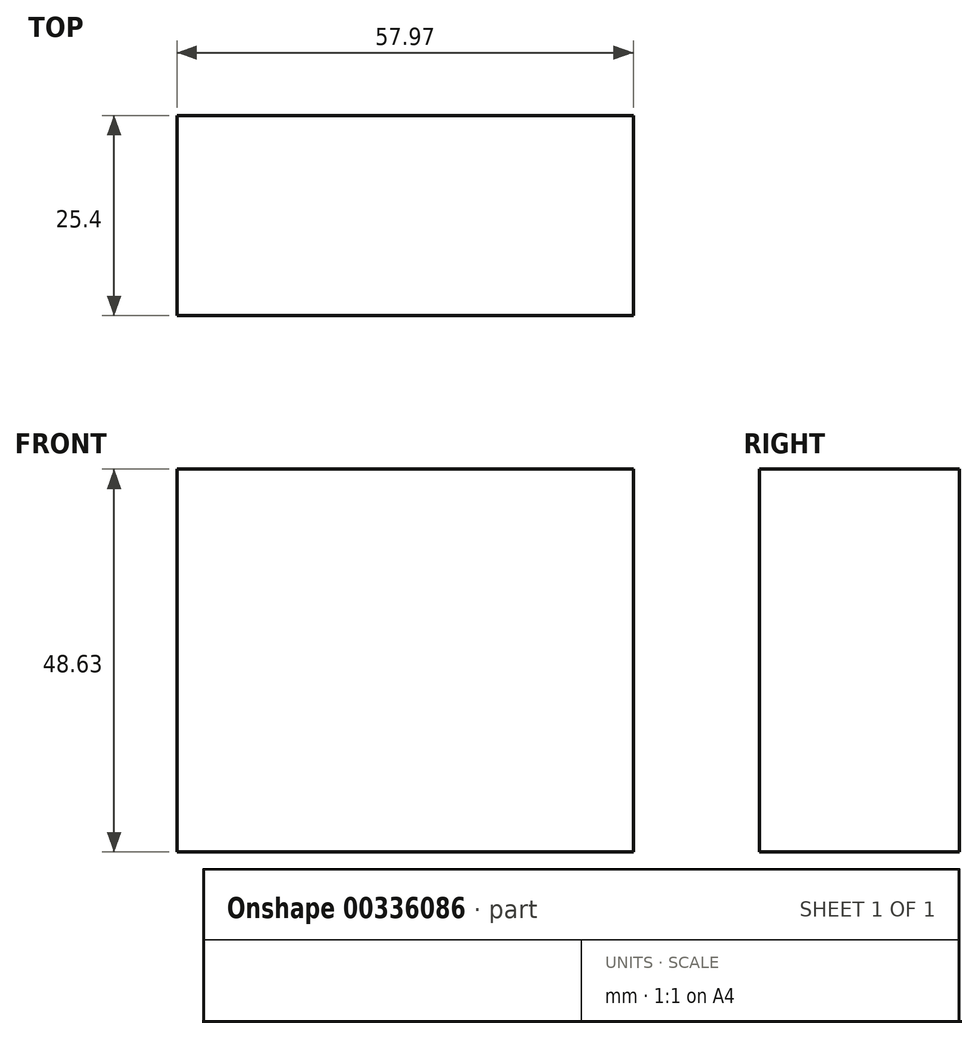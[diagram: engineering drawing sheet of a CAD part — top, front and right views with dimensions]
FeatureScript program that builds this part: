
annotation { "Feature Type Name" : "Feature", "Feature Type Description" : "" }
export const myFeature = defineFeature(function(context is Context, id is Id, definition is map)
    precondition{}
    {
        {
            var Q0;
            Q0=qCreatedBy(makeId("Front.planeOp"),FACE);
            var sketch = newSketch(context, id + "F0", { "sketchPlane" : qUnion([Q0])});
            skLineSegment(sketch, "E0.bottom", {"start": v(-29.7, 24.91) * mm, "end": v(28.27, 24.91) * mm});
            skLineSegment(sketch, "E0.top", {"start": v(-29.7, -23.72) * mm, "end": v(28.27, -23.72) * mm});
            skLineSegment(sketch, "E0.left", {"start": v(-29.7, 24.91) * mm, "end": v(-29.7, -23.72) * mm});
            skLineSegment(sketch, "E0.right", {"start": v(28.27, 24.91) * mm, "end": v(28.27, -23.72) * mm});
            skSolve(sketch);
        }
        {
            var Q0;
            Q0=makeQuery(id+"F0.imprint","IMPRINT",FACE,{"disambiguationData":[TD([[makeQuery(id+"F0.imprint","IMPRINT",EDGE,{"derivedFrom":sQuery(id+"F0.wireOp",EDGE,"E0.bottom")}),-1.0]])]});
            extrude(context, id + "F1", {"entities" : qUnion([Q0]), "depth" : 25.4 * mm});
        }
    });
